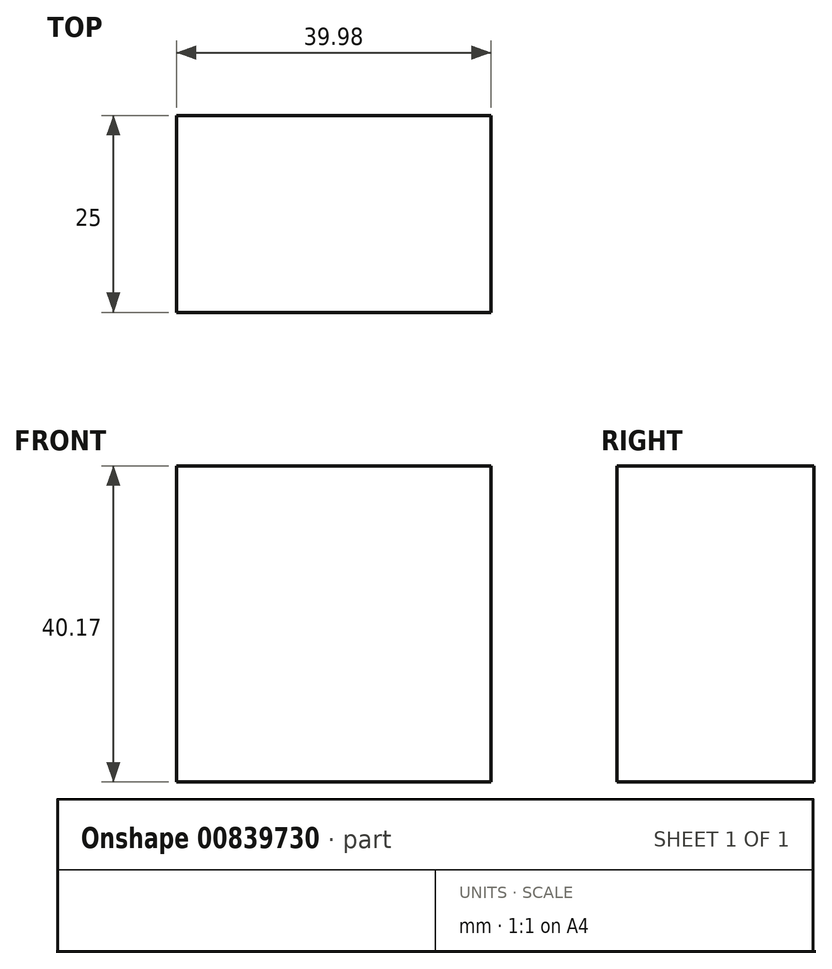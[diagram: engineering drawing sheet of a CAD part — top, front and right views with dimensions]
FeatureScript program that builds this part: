
annotation { "Feature Type Name" : "Feature", "Feature Type Description" : "" }
export const myFeature = defineFeature(function(context is Context, id is Id, definition is map)
    precondition{}
    {
        {
            var Q0;
            Q0=qCreatedBy(makeId("Front.planeOp"),FACE);
            var sketch = newSketch(context, id + "F0", { "sketchPlane" : qUnion([Q0])});
            skLineSegment(sketch, "E0.bottom", {"start": v(-139.9, 24.17) * mm, "end": v(-99.93, 24.17) * mm});
            skLineSegment(sketch, "E0.top", {"start": v(-139.9, -16) * mm, "end": v(-99.93, -16) * mm});
            skLineSegment(sketch, "E0.left", {"start": v(-139.9, 24.17) * mm, "end": v(-139.9, -16) * mm});
            skLineSegment(sketch, "E0.right", {"start": v(-99.93, 24.17) * mm, "end": v(-99.93, -16) * mm});
            skSolve(sketch);
        }
        {
            var Q0;
            Q0 = qSketchRegion(id + "F0", true);
            extrude(context, id + "F1", {"entities" : qUnion([Q0]), "depth" : 25 * mm, "offsetDistance" : 25 * mm});
        }
    });
